# Revit family: Chair-Multi-Purpose-Allermuir-ADL12
name_source: partatom
category: Furniture
revit_build: Autodesk Revit Architecture 2012 (Build: 20110309_2315(x64)
units: mm (PartAtom-declared; Revit-internal decimal feet)

## types (1)
- ADL12
    04 CSI = 12 51 00
    2.5" Casters = No
    95 CSI = 12510
    Advanced Sync Tilt with Multi Position Back = No
    Assembly Code = E2020200
    Back = Plastic - Allermuir - Black
    Base = Metal - Allermuir - Polished Aluminum
    Base Type = 4 leg frame
    Base or Frame = Tubular Steel Frame in Silver EPPC
    Black GRP Base = No
    Black Gas Lift = No
    Brochure URL = http://www.allermuir.net
    CAD Blocks URL = http://www.allermuir.net
    Color Availability = See price list for material options
    Description = 4 leg frame plastic seat & back
    Fabric Spec Sheets = http://www.allermuir.net
    Glides = Plastic - Allermuir - Black
    Height Adjustable Arms = No
    Height Adjustable Arms with Multi funtction Pad = No
    LEED Stats URL = http://www.allermuir.net
    Manufacturer = Allermuir
    Manufacturer Fax = (419) 887 5805
    Model = ADL12
    Negative Seat Tilt = No
    Overall Depth = 20 "
    Overall Height = 31 "
    Overall Width = 19 "
    Pedestal Base = NO
    Plastic Arms in Black = NO
    Plugin Data URL = http://products.ecoscorecard.com
    Polished Aluminum Base = No
    Pricing URL = http://www.allermuir.net
    Product Line = Ad-Lib
    Product Page URL = http://www.allermuir.net
    Seat Depth = 18 "
    Seat Depth Adjustment = No
    Seat Height = 19 "
    Seat Width = 16 "
    Seat or Base = Fabric - Allermuir - Hue-Black
    Slimline Upholstery = No
    Specifications URL = http://www.allermuir.net
    Stacks = Yes
    Subcategory = Multi-Purpose Line
    Swaged Tubular Steel Legs = YES
    URL = http://www.allermuir.net
    Upholstered Back = NO
    Upholstered Seat = NO
    Weight = 10.7 lb
    ecoScorecard Product Page = http://products.ecoscorecard.com
    ecoScorecard_data = http://thesenatorgroup.ecoscorecard.com

## geometry (parser evidence)
native form markers: Blend x6, Sweep x5
no freeform markers — native parametric forms only
